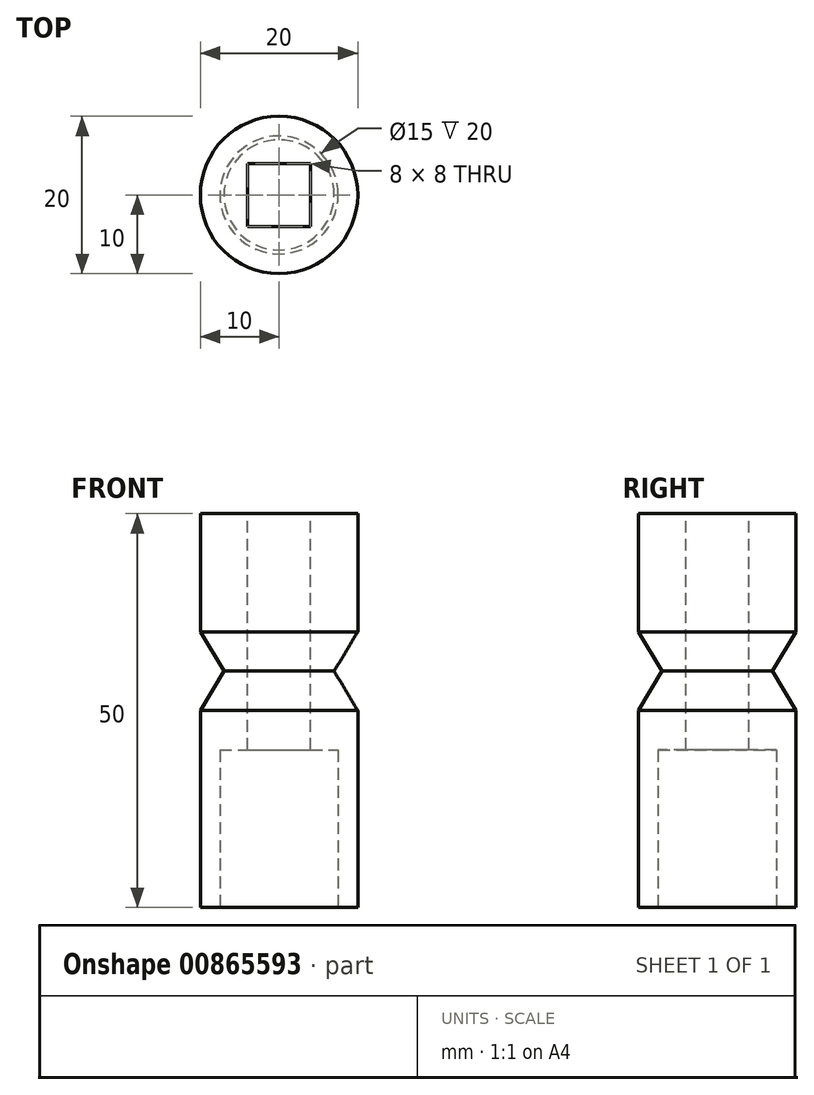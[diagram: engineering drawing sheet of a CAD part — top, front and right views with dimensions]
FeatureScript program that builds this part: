
annotation { "Feature Type Name" : "Feature", "Feature Type Description" : "" }
export const myFeature = defineFeature(function(context is Context, id is Id, definition is map)
    precondition{}
    {
        {
            var Q0;
            Q0=qCreatedBy(makeId("Top.planeOp"),FACE);
            var sketch = newSketch(context, id + "F0", { "sketchPlane" : qUnion([Q0])});
            skCircle(sketch, "E0", {"center": v(0, 0) * mm, "radius": 10 * mm});
            skSolve(sketch);
        }
        {
            var Q0;
            Q0 = qSketchRegion(id + "F0", true);
            extrude(context, id + "F1", {"entities" : qUnion([Q0]), "endBound" : BoundingType.SYMMETRIC, "depth" : 50 * mm, "offsetDistance" : 25 * mm});
        }
        {
            var Q0;
            Q0=makeQuery(id+"F1.opExtrude","CAP_FACE",FACE,{"disambiguationData":[OSD([sQuery(id+"F0.wireOp",EDGE,"E0")])],"isStart":false});
            var sketch = newSketch(context, id + "F2", { "sketchPlane" : qUnion([Q0])});
            skLineSegment(sketch, "E1.bottom", {"start": v(-4, 4) * mm, "end": v(4, 4) * mm});
            skLineSegment(sketch, "E1.top", {"start": v(-4, -4) * mm, "end": v(4, -4) * mm});
            skLineSegment(sketch, "E1.left", {"start": v(-4, 4) * mm, "end": v(-4, -4) * mm});
            skLineSegment(sketch, "E1.right", {"start": v(4, 4) * mm, "end": v(4, -4) * mm});
            skPoint(sketch, "E1.middle", {"position": v(0, 0) * mm});
            skSolve(sketch);
        }
        {
            var Q0;
            Q0 = qSketchRegion(id + "F2", true);
            extrude(context, id + "F3", {"entities" : qUnion([Q0]), "operationType" : NewBodyOperationType.REMOVE, "endBound" : BoundingType.THROUGH_ALL, "oppositeDirection" : true, "depth" : 25 * mm, "offsetDistance" : 25 * mm});
        }
        {
            var Q0;
            Q0=qCreatedBy(makeId("Front.planeOp"),FACE);
            var sketch = newSketch(context, id + "F4", { "sketchPlane" : qUnion([Q0])});
            skLineSegment(sketch, "E2.bottom", {"start": v(-10, 25) * mm, "end": v(10, 25) * mm, "construction": true});
            skLineSegment(sketch, "E2.top", {"start": v(-10, -25) * mm, "end": v(10, -25) * mm, "construction": true});
            skLineSegment(sketch, "E2.left", {"start": v(-10, 25) * mm, "end": v(-10, -25) * mm, "construction": true});
            skLineSegment(sketch, "E2.right", {"start": v(10, 25) * mm, "end": v(10, -25) * mm, "construction": true});
            skPoint(sketch, "E2.middle", {"position": v(0, 0) * mm});
            skLineSegment(sketch, "E3.left", {"start": v(-10, 0) * mm, "end": v(-10, 10) * mm});
            skLineSegment(sketch, "E4", {"start": v(-10, 0) * mm, "end": v(-7, 5) * mm});
            skLineSegment(sketch, "E5", {"start": v(-7, 5) * mm, "end": v(-10, 10) * mm});
            skSolve(sketch);
        }
        {
            var Q0;
            Q0=qCreatedBy(makeId("Front.planeOp"),FACE);
            var sketch = newSketch(context, id + "F5", { "sketchPlane" : qUnion([Q0])});
            skLineSegment(sketch, "E6", {"start": v(0, 0) * mm, "end": v(0, 20.24) * mm});
            skSolve(sketch);
        }
        {
            var Q0;
            Q0 = qSketchRegion(id + "F4", true);
            var Q1;
            Q1=sQuery(id+"F5.wireOp",EDGE,"E6");
            revolve(context, id + "F6", {"operationType" : NewBodyOperationType.REMOVE, "surfaceOperationType" : NewSurfaceOperationType.NEW, "entities" : qUnion([Q0]), "axis" : qUnion([Q1]), "revolveType" : RevolveType.FULL, "oppositeDirection" : true});
        }
        {
            var Q0;
            Q0=makeQuery(id+"F1.opExtrude","CAP_FACE",FACE,{"disambiguationData":[OSD([sQuery(id+"F0.wireOp",EDGE,"E0")])],"isStart":true});
            var sketch = newSketch(context, id + "F7", { "sketchPlane" : qUnion([Q0])});
            skCircle(sketch, "E7", {"center": v(0, 0) * mm, "radius": 7.5 * mm});
            skSolve(sketch);
        }
        {
            var Q0;
            Q0 = qSketchRegion(id + "F7", true);
            extrude(context, id + "F8", {"entities" : qUnion([Q0]), "operationType" : NewBodyOperationType.REMOVE, "oppositeDirection" : true, "depth" : 20 * mm, "offsetDistance" : 25 * mm});
        }
    });
